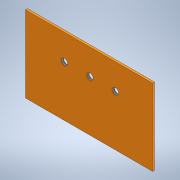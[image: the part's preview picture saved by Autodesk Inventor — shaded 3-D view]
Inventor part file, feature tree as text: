
AUTODESK INVENTOR PART (.ipt)
format: ipt  version: 2021 (Build 250183000, 183)  size: 117,248 bytes
history: native  units: in
note: dims shown in document units (in); Inventor stores cm internally (conversion verified against a paired STEP export)
features: extrude x2, sketch x2, pattern_linear x1, projected_geometry x1
ambient origin geometry x8: Origin, YZ Plane, XZ Plane, XY Plane, X Axis, Y Axis, Z Axis, Center Point
bodies: Solid1 (feature_tree)
feature tree (6):
  extrude  "Extrusion1"  Depth=0.004in TaperAngle=0.0deg
  extrude  "Extrusion2"  Depth=0.0728in
  pattern_linear  "Rectangular Pattern1"  Spacing1=0.0in  [1 undecoded]
  sketch  "Sketch1"  dims[d0=0.25in d2=0.004in d3=0.0in]
  sketch  "Sketch2"  dims[d4=0.012in d5=0.0728in d6=0.0in d7=0.0in d8=1.1811in d10=0.05in d12=0.1in d14=0.05in]
  projected_geometry  "Projected Loop1"
note: 1 required parameter value undecoded (feature->parameter linkage not recoverable at this tier; creation-order binding heuristic only, values carry confidence <= 0.55)
